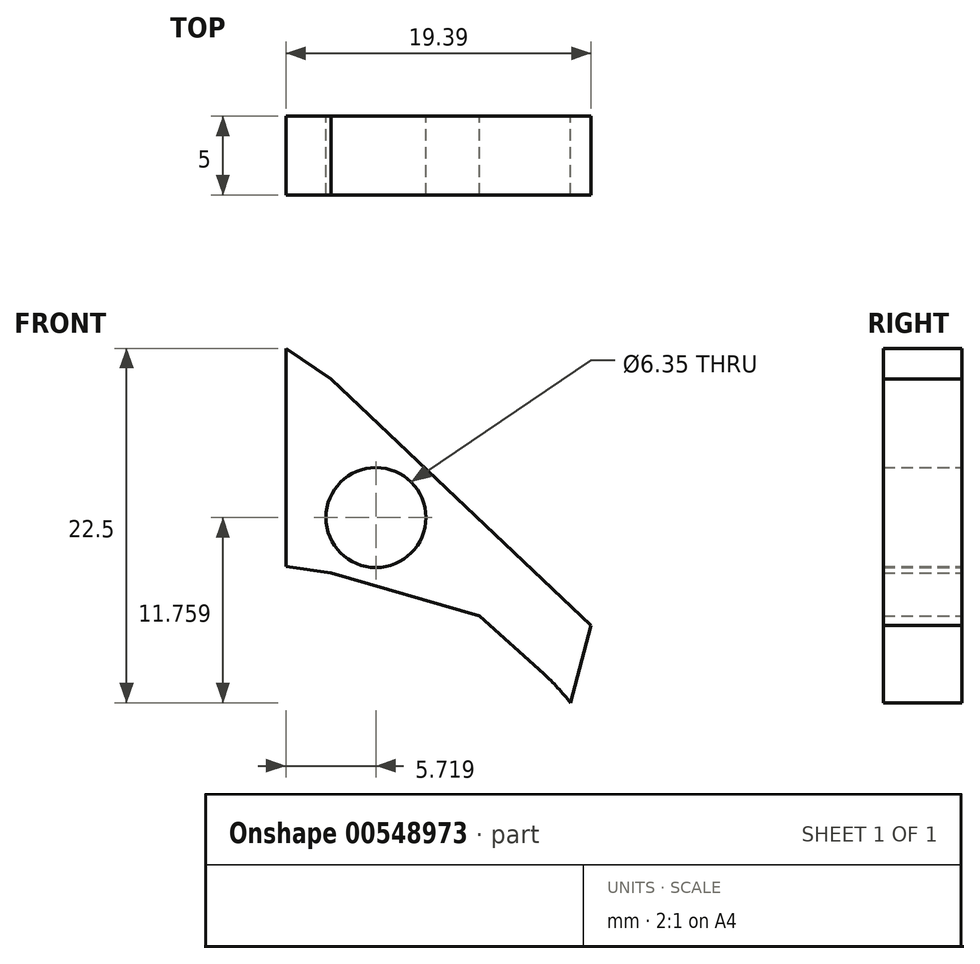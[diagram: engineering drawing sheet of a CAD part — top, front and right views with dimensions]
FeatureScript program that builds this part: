
annotation { "Feature Type Name" : "Feature", "Feature Type Description" : "" }
export const myFeature = defineFeature(function(context is Context, id is Id, definition is map)
    precondition{}
    {
        {
            var Q0;
            Q0=qCreatedBy(makeId("Front.planeOp"),FACE);
            var sketch = newSketch(context, id + "F0", { "sketchPlane" : qUnion([Q0])});
            skArc(sketch, "E0", {"start": v(-11.66, 35.76) * mm, "mid": v(-12.46, 36.71) * mm, "end": v(-13.35, 37.59) * mm});
            skLineSegment(sketch, "E1.4.11.0", {"start": v(-11.66, 35.76) * mm, "end": v(-10.34, 40.67) * mm});
            skLineSegment(sketch, "E2", {"start": v(-10.34, 40.67) * mm, "end": v(-26.88, 56.33) * mm});
            skLineSegment(sketch, "E3", {"start": v(-26.88, 43.99) * mm, "end": v(-17.44, 41.28) * mm});
            skLineSegment(sketch, "E4", {"start": v(-17.44, 41.28) * mm, "end": v(-13.35, 37.59) * mm});
            skCircle(sketch, "E5", {"center": v(-24.01, 47.52) * mm, "radius": 3.18 * mm});
            skLineSegment(sketch, "E6", {"start": v(-26.88, 43.99) * mm, "end": v(-29.73, 44.4) * mm});
            skLineSegment(sketch, "E7", {"start": v(-29.73, 44.4) * mm, "end": v(-29.73, 58.26) * mm});
            skLineSegment(sketch, "E8", {"start": v(-29.73, 58.26) * mm, "end": v(-26.88, 56.33) * mm});
            skSolve(sketch);
        }
        {
            var Q0;
            Q0=makeQuery(id+"F0.imprint","IMPRINT",FACE,{"disambiguationData":[TD([[makeQuery(id+"F0.imprint","IMPRINT",EDGE,{"derivedFrom":sQuery(id+"F0.wireOp",EDGE,"E0")}),-1.0]])]});
            extrude(context, id + "F1", {"entities" : qUnion([Q0]), "depth" : 5 * mm, "offsetDistance" : 25.4 * mm});
        }
    });
